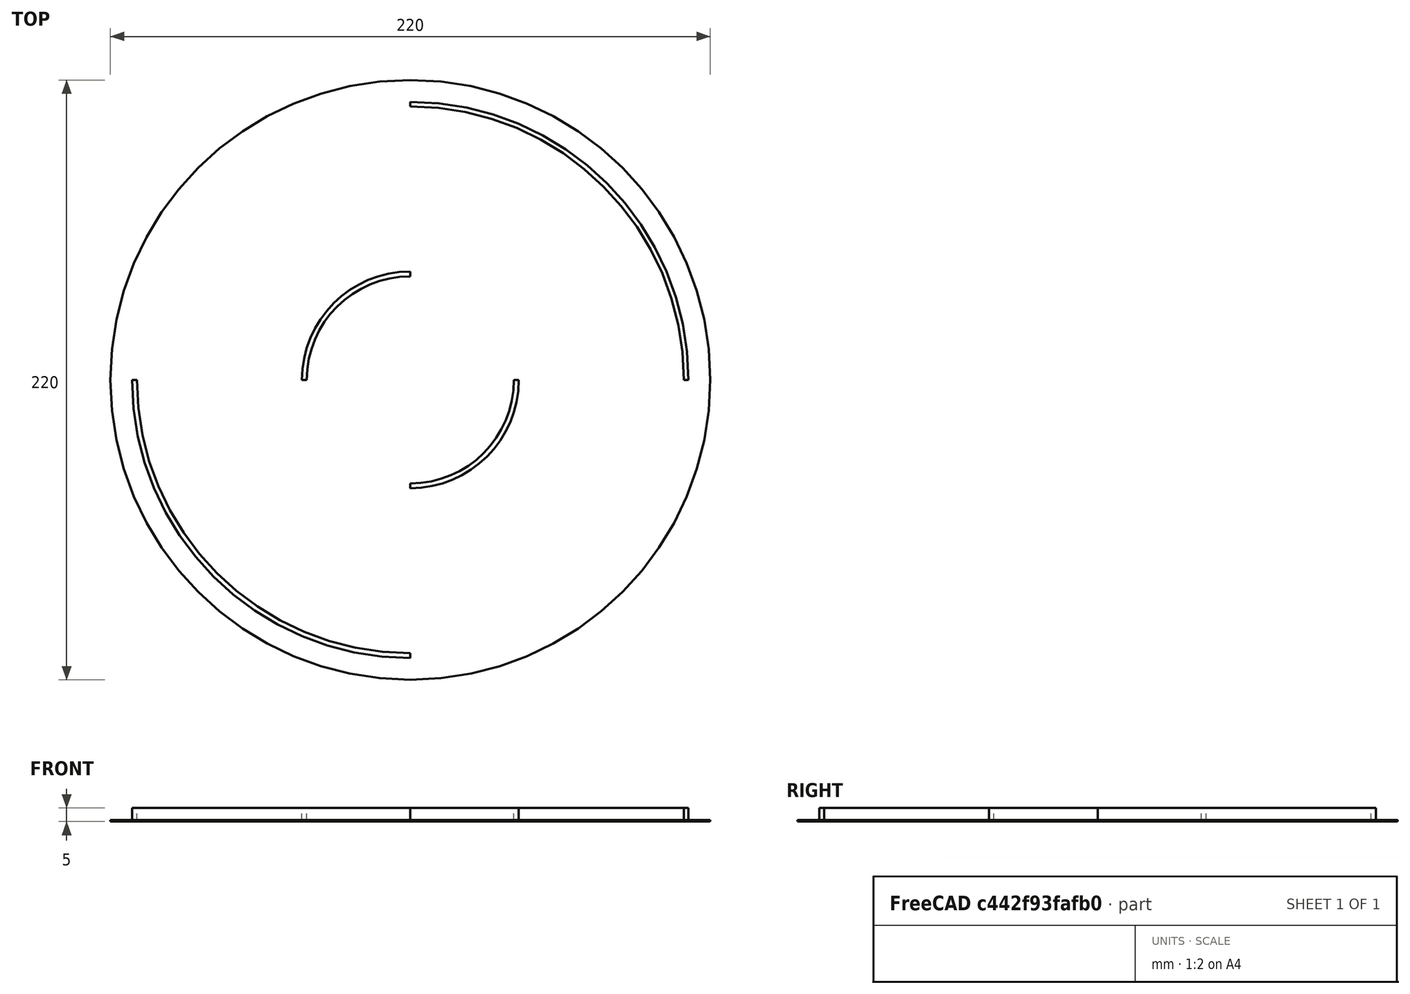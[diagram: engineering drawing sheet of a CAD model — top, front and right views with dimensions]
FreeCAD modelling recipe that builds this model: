
FCSTD DOCUMENT  (FreeCAD 0.18.4R)
Label: disco
License: All rights reserved
LicenseURL: http://en.wikipedia.org/wiki/All_rights_reserved
objects: Part::Cylinder×9, Part::Cut×4
note: 13 computed .brp shape members not serialized (recipe doc carries the construction recipe); baked Part::Feature solids carry a one-line shape summary decoded from their .brp

FEATURE [Part::Cylinder] Cylinder  label="Cilindro"
  Angle = 360
  AttacherType = Attacher::AttachEngine3D
  Height = 0.6
  Radius = 110
FEATURE [Part::Cylinder] Cylinder001  label="Cilindro001"
  Angle = 90
  AttacherType = Attacher::AttachEngine3D
  Height = 5
  Radius = 102
FEATURE [Part::Cylinder] Cylinder002  label="Cilindro002"
  Angle = 90
  AttacherType = Attacher::AttachEngine3D
  Height = 5
  Radius = 100.25
FEATURE [Part::Cut] Cut
  Base = -> Cylinder001
  Tool = -> Cylinder002
FEATURE [Part::Cylinder] Cylinder012  label="Cilindro012"
  Angle = 90
  AttacherType = Attacher::AttachEngine3D
  Height = 5
  Radius = 38
FEATURE [Part::Cylinder] Cylinder013  label="Cilindro013"
  Angle = 90
  AttacherType = Attacher::AttachEngine3D
  Height = 5
  Radius = 39.75
FEATURE [Part::Cut] Cut007
  Base = -> Cylinder013
  Placement = pos=(0,0,0) rot=(0,0,1;1.5708rad)
  Tool = -> Cylinder012
FEATURE [Part::Cylinder] Cylinder014  label="Cilindro014"
  Angle = 90
  AttacherType = Attacher::AttachEngine3D
  Height = 5
  Radius = 102
FEATURE [Part::Cylinder] Cylinder015  label="Cilindro015"
  Angle = 90
  AttacherType = Attacher::AttachEngine3D
  Height = 5
  Radius = 100.25
FEATURE [Part::Cut] Cut008
  Base = -> Cylinder014
  Placement = pos=(0,0,0) rot=(0,0,1;3.14159rad)
  Tool = -> Cylinder015
FEATURE [Part::Cylinder] Cylinder016  label="Cilindro016"
  Angle = 90
  AttacherType = Attacher::AttachEngine3D
  Height = 5
  Radius = 38
FEATURE [Part::Cylinder] Cylinder017  label="Cilindro017"
  Angle = 90
  AttacherType = Attacher::AttachEngine3D
  Height = 5
  Radius = 39.75
FEATURE [Part::Cut] Cut009
  Base = -> Cylinder017
  Placement = pos=(0,0,0) rot=(0,0,1;4.71239rad)
  Tool = -> Cylinder016
